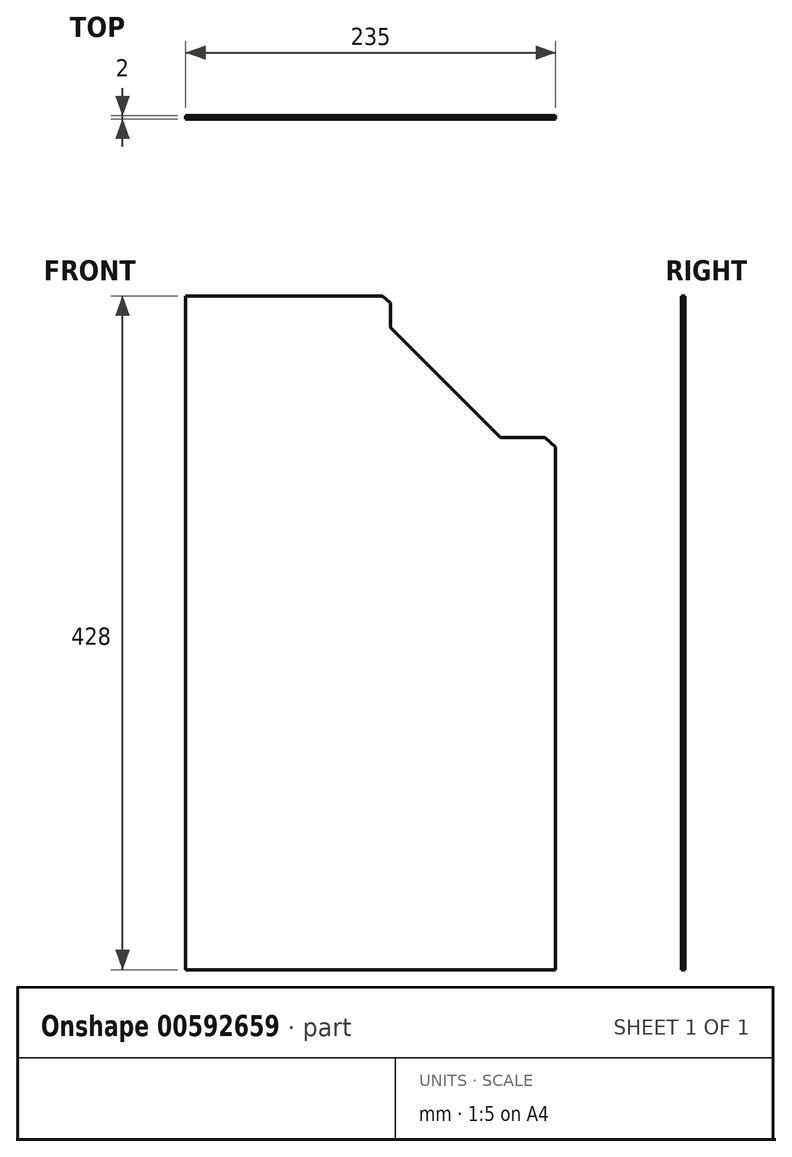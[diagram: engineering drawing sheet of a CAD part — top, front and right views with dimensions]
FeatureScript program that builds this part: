
annotation { "Feature Type Name" : "Feature", "Feature Type Description" : "" }
export const myFeature = defineFeature(function(context is Context, id is Id, definition is map)
    precondition{}
    {
        {
            var Q0;
            Q0=qCreatedBy(makeId("Front.planeOp"),FACE);
            var sketch = newSketch(context, id + "F0", { "sketchPlane" : qUnion([Q0])});
            skLineSegment(sketch, "E0.bottom", {"start": v(-129.08, 332.54) * mm, "end": v(105.92, 332.54) * mm});
            skLineSegment(sketch, "E0.top", {"start": v(-129.08, -95.46) * mm, "end": v(105.92, -95.46) * mm});
            skLineSegment(sketch, "E0.left", {"start": v(-129.08, 332.54) * mm, "end": v(-129.08, -95.46) * mm});
            skLineSegment(sketch, "E0.right", {"start": v(105.92, 332.54) * mm, "end": v(105.92, -95.46) * mm});
            skSolve(sketch);
        }
        {
            var Q0;
            Q0 = qSketchRegion(id + "F0", true);
            extrude(context, id + "F1", {"entities" : qUnion([Q0]), "depth" : 2 * mm, "offsetDistance" : 25 * mm});
        }
        {
            var Q0;
            Q0=makeQuery(id+"F1.opExtrude","SWEPT_EDGE",EDGE,{"disambiguationData":[OSD([sQuery(id+"F0.wireOp",EDGE,"E0.bottom"),sQuery(id+"F0.wireOp",EDGE,"E0.right")])]});
            chamfer(context, id + "F2", {"entities" : qUnion([Q0]), "chamferType" : ChamferType.TWO_OFFSETS, "width1" : 110 * mm, "oppositeDirection" : false, "width2" : 96 * mm, "tangentPropagation" : true});
        }
        {
            var Q0;
            Q0=makeQuery(id+"F1.opExtrude","CAP_FACE",FACE,{"disambiguationData":[OSD([sQuery(id+"F0.wireOp",EDGE,"E0.bottom"),sQuery(id+"F0.wireOp",EDGE,"E0.top"),sQuery(id+"F0.wireOp",EDGE,"E0.left"),sQuery(id+"F0.wireOp",EDGE,"E0.right")])],"isStart":false});
            var sketch = newSketch(context, id + "F3", { "sketchPlane" : qUnion([Q0])});
            skLineSegment(sketch, "E1", {"start": v(0.92, 328.18) * mm, "end": v(0.92, 312.54) * mm});
            skLineSegment(sketch, "E2", {"start": v(0.92, 312.54) * mm, "end": v(70.92, 242.54) * mm});
            skLineSegment(sketch, "E3", {"start": v(99.04, 242.54) * mm, "end": v(70.92, 242.54) * mm});
            skPoint(sketch, "E4.orphan", {"position": v(76.92, 236.54) * mm});
            skLineSegment(sketch, "E5", {"start": v(0.92, 328.18) * mm, "end": v(99.04, 242.54) * mm});
            skSolve(sketch);
        }
        {
            var Q0;
            Q0 = qSketchRegion(id + "F3", true);
            extrude(context, id + "F4", {"entities" : qUnion([Q0]), "operationType" : NewBodyOperationType.REMOVE, "oppositeDirection" : true, "depth" : 25 * mm, "offsetDistance" : 25 * mm});
        }
    });
